# Revit family: Hand_Shower-GROHE-Euphoria_Cosmopolitan-26466_Series
name_source: partatom
category: Plumbing Fixtures
units: mm (PartAtom-declared; Revit-internal decimal feet)

## family parameters
Always vertical = No
Cut with Voids When Loaded = No
OmniClass Number = 23.45.05.14.17
OmniClass Title = Showers
Part Type = Normal
Room Calculation Point = No
Round Connector Dimension = Use Diameter
Shared = Yes
Work Plane-Based = Yes

## types (1)
- 26466000
    Assembly Code = D2010710
    CEC Compliant = Yes
    CW Connection = No
    CWFU = 3
    CalGreen Compliant = Yes
    Default Elevation = 0"
    Description = Euphoria Cosmopolitan Stick
    Diameter = 1/2"
    Finish = Metal-Grohe-000-Chrome
    Flow Rate = 1.75 gpm (6.6 l/min)
    HW Connection = No
    HWFU = 3
    Height = 8 1/2"
    IAPMO Compliance = WaterSense /CEC Certified /CALGreen Compliant/ Massachusetts Plumbing Board Approved/ Energy Policy Act of 1992 /CSA B125.1 /ASME A112.18.1
    Manufacturer = Grohe
    Material = Metal-Grohe-000-Chrome
    Model = 26466000
    Orifice Material = Rubber-Grohe-Grey
    Price = Prices may vary. Please consult Manufacturer Representative for most up-to-date price list.
    Product Documentation Link = https://americanstandard.box.com
    Product Page URL = https://www.grohe.us
    Revised Date = 08/04/2022
    Tempered Connection Diameter = 1/2"
    Tempered Connection Radius = 1/4"
    Tempered Water Connection = Yes
    URL = https://www.grohe.us
    Vent Connection = No
    WFU = 4
    Waste Connection = No

## geometry (parser evidence)
native form markers: Sweep x2
no freeform markers — native parametric forms only
